# Revit family: ledapollo-e4_rd450-11_22w-dim-827_840_520034068200_a44f
name_source: partatom
category: Lighting Fixtures
units: mm (PartAtom-declared; Revit-internal decimal feet)

## family parameters
Cut with Voids When Loaded = No
Host = Face
Light Source = No
Part Type = Normal
Room Calculation Point = No
Round Connector Dimension = Use Diameter
Shared = No

## types (1)
- LEDApollo-E4 Rd450-11/22W-DIM-827/840 (1 x LED, 2200 lm, 4000)
    Apparent Load = 11 VA
    Approval mark = CE
    CIE Flux Codes = 42 73 92 91 100
    Color Rendering = 80
    Color Temperature = 4000
    Control Gear = Electronic ballast
    Default Elevation = 1800 mm
    Description = Ceiling Light Apollo G4 Ø450mm-22W-1100/2200lm2700/4000K-Triac
    Frequency = 60 Hz
    Height = 68 mm
    Lamp = 1 x LED
    Lamp Light Flux = 2200 lm
    Lamp count = 1
    Length = 450 mm
    Luminous efficacy = 200 lm/W
    Manufacturer = OPPLE
    ModVariant = No
    Model = 520034068200
    Number of Poles = 1
    OnlyDefault = Yes
    Power Factor = 1
    Product Name = LEDApollo-E4 Rd450-11/22W-DIM-827/840
    Product group = Ceiling / wall-mounted luminaires
    ProductGroupID = 30
    Protection Class = Protection class II
    Protection Degree = IP 44
    RLX_Detail_Level = 1
    RLX_Emergency_Light_Flux = 0 lm
    RLX_Emergency_Type = 0
    RLX_Emergency_Type_DB = No
    RlxData = <blob elided: 173181 chars, md5=c14cbdb1>
    Socket = socket
    Standby Power = 0 W
    System Light Flux = 2196 lm
    System Power = 11 W
    Type Comments = Product without accessories
    Type Image = web_apollo_e4.jpg
    URL = http://relux.com
    VarID = ---
    Voltage = 230 V
    Voltage Range = 220-240 V
    Weight = 0.00 kg
    Width = 450 mm

## geometry (parser evidence)
native form markers: Blend x4, Sweep x10
no freeform markers — native parametric forms only
